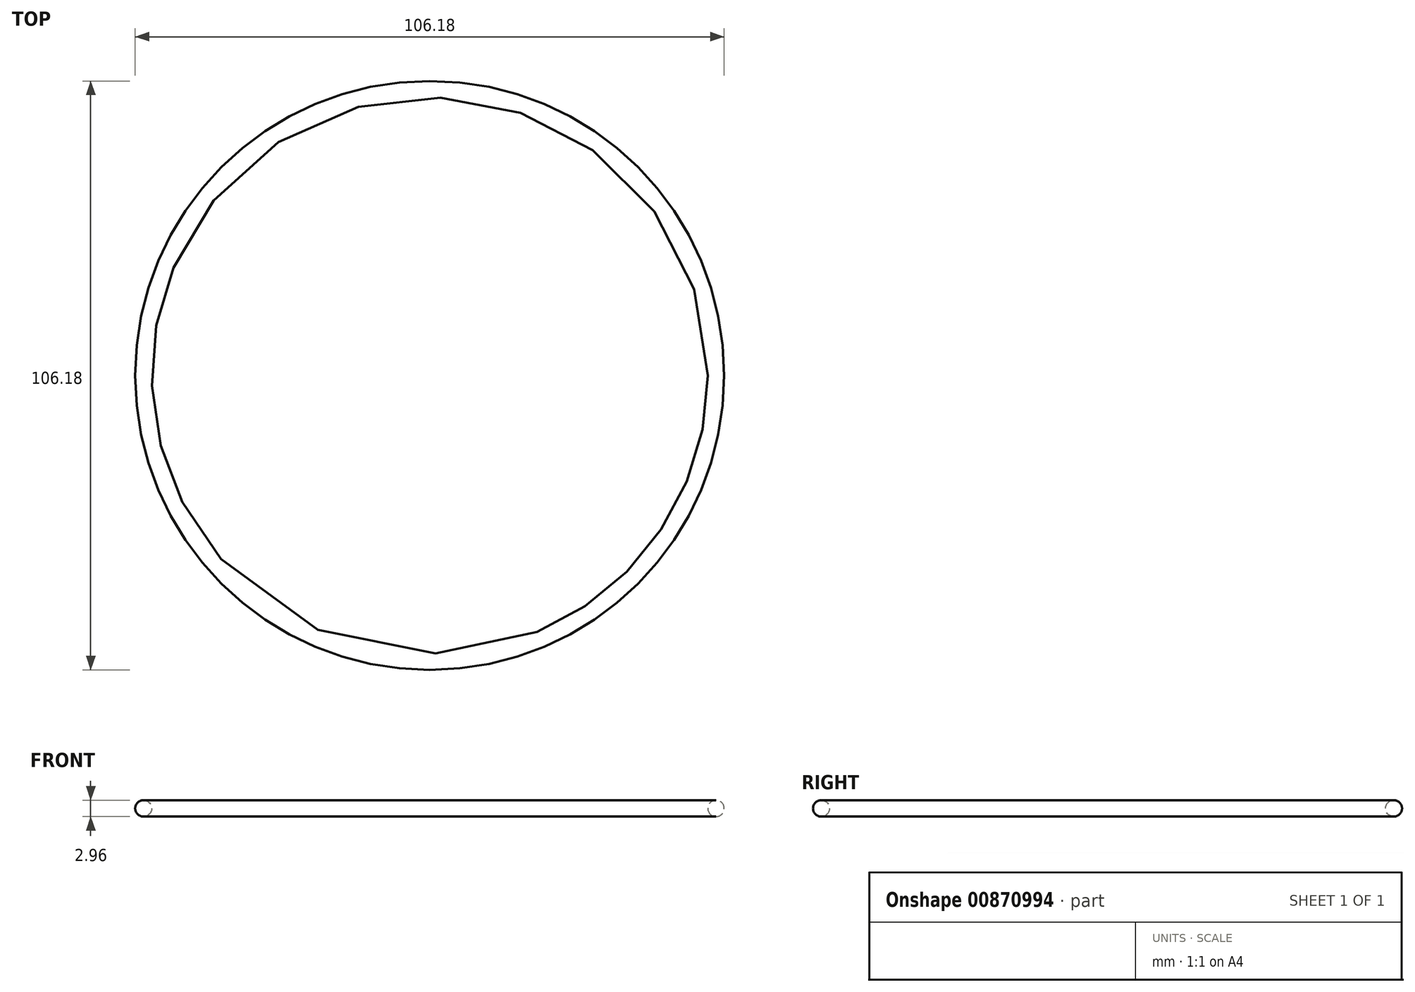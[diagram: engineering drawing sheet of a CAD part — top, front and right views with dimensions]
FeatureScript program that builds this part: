
annotation { "Feature Type Name" : "Feature", "Feature Type Description" : "" }
export const myFeature = defineFeature(function(context is Context, id is Id, definition is map)
    precondition{}
    {
        {
            var Q0;
            Q0=qCreatedBy(makeId("Top.planeOp"),FACE);
            var sketch = newSketch(context, id + "F0", { "sketchPlane" : qUnion([Q0])});
            skCircle(sketch, "E0", {"center": v(0, 0) * mm, "radius": 51.62 * mm});
            skSolve(sketch);
        }
        {
            var Q0;
            Q0=qCreatedBy(makeId("Right.planeOp"),FACE);
            var sketch = newSketch(context, id + "F1", { "sketchPlane" : qUnion([Q0])});
            skCircle(sketch, "E1", {"center": v(51.6, 0) * mm, "radius": 1.48 * mm});
            skSolve(sketch);
        }
        {
            var Q0;
            Q0=makeQuery(id+"F1.imprint","IMPRINT",FACE,{"disambiguationData":[TD([[makeQuery(id+"F1.imprint","IMPRINT",EDGE,{"derivedFrom":sQuery(id+"F1.wireOp",EDGE,"E1")}),1.0]])]});
            var Q1;
            Q1=sQuery(id+"F0.wireOp",EDGE,"E0");
            sweep(context, id + "F2", {"profiles" : qUnion([Q0]), "path" : qUnion([Q1])});
        }
    });
